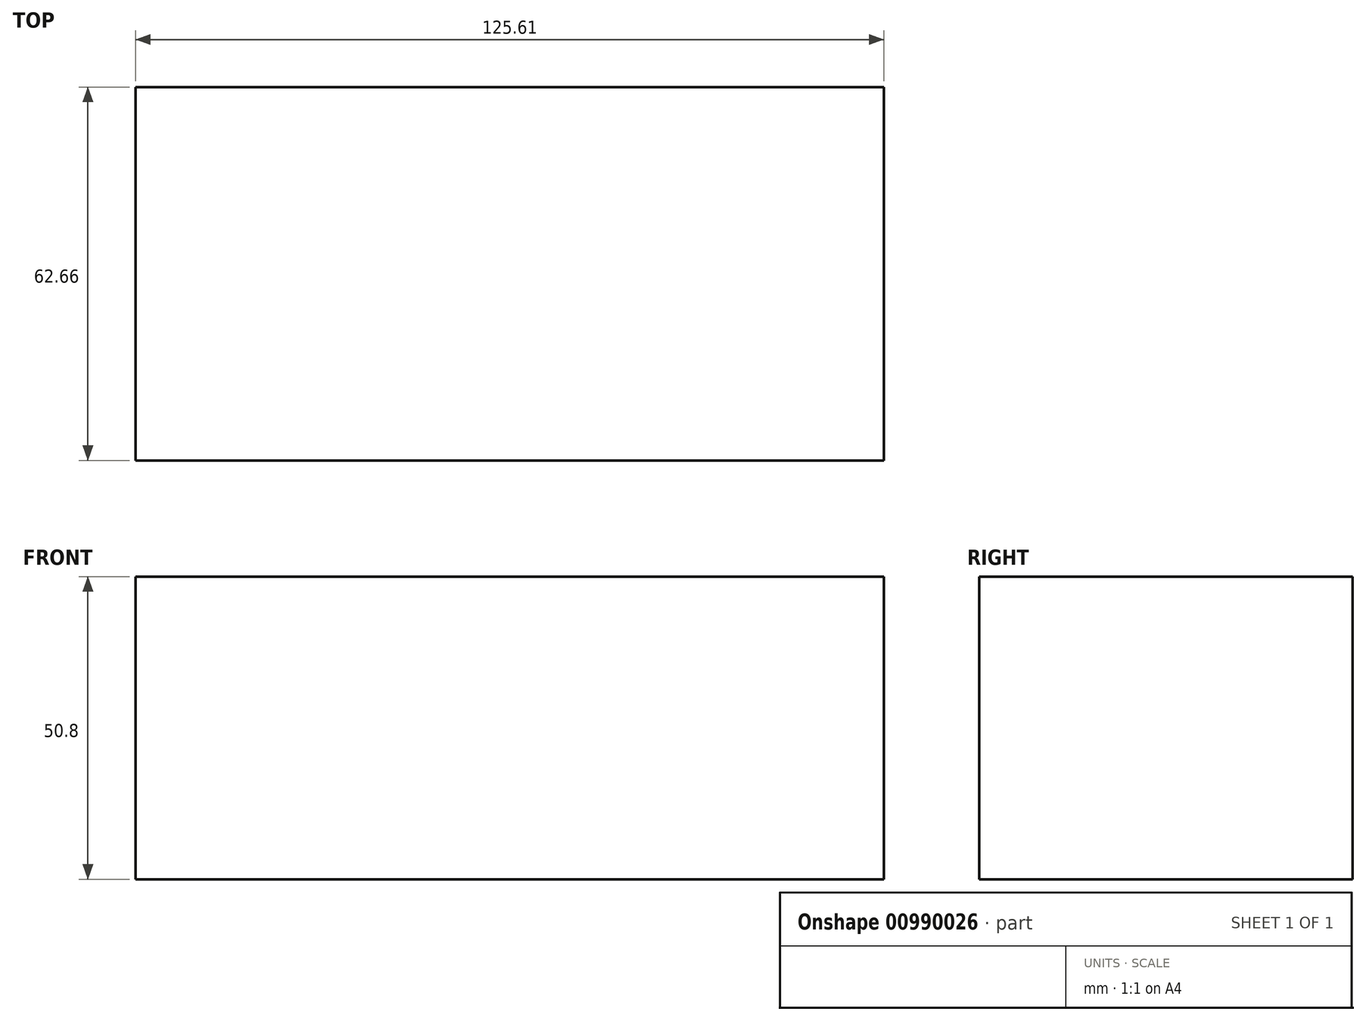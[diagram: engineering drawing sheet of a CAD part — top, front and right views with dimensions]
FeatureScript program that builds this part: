
annotation { "Feature Type Name" : "Feature", "Feature Type Description" : "" }
export const myFeature = defineFeature(function(context is Context, id is Id, definition is map)
    precondition{}
    {
        {
            var Q0;
            Q0=qCreatedBy(makeId("Top.planeOp"),FACE);
            var sketch = newSketch(context, id + "F0", { "sketchPlane" : qUnion([Q0])});
            skLineSegment(sketch, "E0.bottom", {"start": v(73.13, 0) * mm, "end": v(-52.48, 0) * mm});
            skLineSegment(sketch, "E0.top", {"start": v(73.13, -62.66) * mm, "end": v(-52.48, -62.66) * mm});
            skLineSegment(sketch, "E0.left", {"start": v(73.13, 0) * mm, "end": v(73.13, -62.66) * mm});
            skLineSegment(sketch, "E0.right", {"start": v(-52.48, 0) * mm, "end": v(-52.48, -62.66) * mm});
            skSolve(sketch);
        }
        {
            var Q0;
            Q0=makeQuery(id+"F0.imprint","IMPRINT",FACE,{"disambiguationData":[TD([[makeQuery(id+"F0.imprint","IMPRINT",EDGE,{"derivedFrom":sQuery(id+"F0.wireOp",EDGE,"E0.bottom")}),1.0]])]});
            extrude(context, id + "F1", {"entities" : qUnion([Q0]), "depth" : 50.8 * mm, "offsetDistance" : 25.4 * mm});
        }
    });
